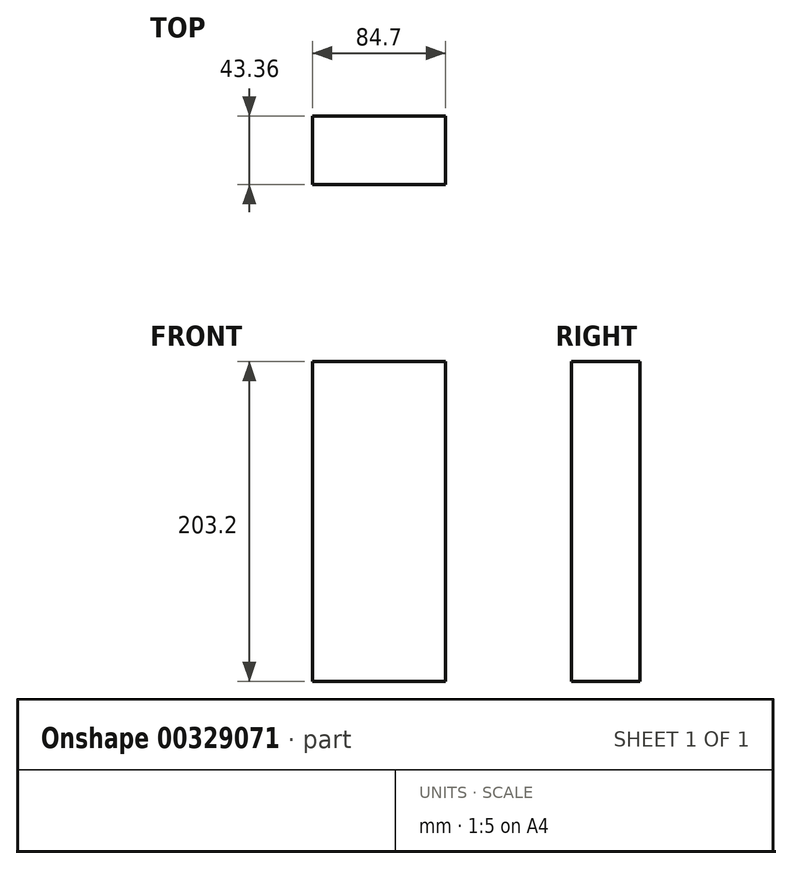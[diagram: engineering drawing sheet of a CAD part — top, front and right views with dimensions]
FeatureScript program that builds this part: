
annotation { "Feature Type Name" : "Feature", "Feature Type Description" : "" }
export const myFeature = defineFeature(function(context is Context, id is Id, definition is map)
    precondition{}
    {
        {
            var Q0;
            Q0=qCreatedBy(makeId("Top.planeOp"),FACE);
            var sketch = newSketch(context, id + "F0", { "sketchPlane" : qUnion([Q0])});
            skLineSegment(sketch, "E0.bottom", {"start": v(44.72, 0) * mm, "end": v(-39.98, 0) * mm});
            skLineSegment(sketch, "E0.top", {"start": v(44.72, -43.36) * mm, "end": v(-39.98, -43.36) * mm});
            skLineSegment(sketch, "E0.left", {"start": v(44.72, 0) * mm, "end": v(44.72, -43.36) * mm});
            skLineSegment(sketch, "E0.right", {"start": v(-39.98, 0) * mm, "end": v(-39.98, -43.36) * mm});
            skSolve(sketch);
        }
        {
            var Q0;
            Q0=makeQuery(id+"F0.imprint","IMPRINT",FACE,{"disambiguationData":[TD([[makeQuery(id+"F0.imprint","IMPRINT",EDGE,{"derivedFrom":sQuery(id+"F0.wireOp",EDGE,"E0.bottom")}),1.0]])]});
            extrude(context, id + "F1", {"entities" : qUnion([Q0]), "depth" : 203.2 * mm});
        }
    });
